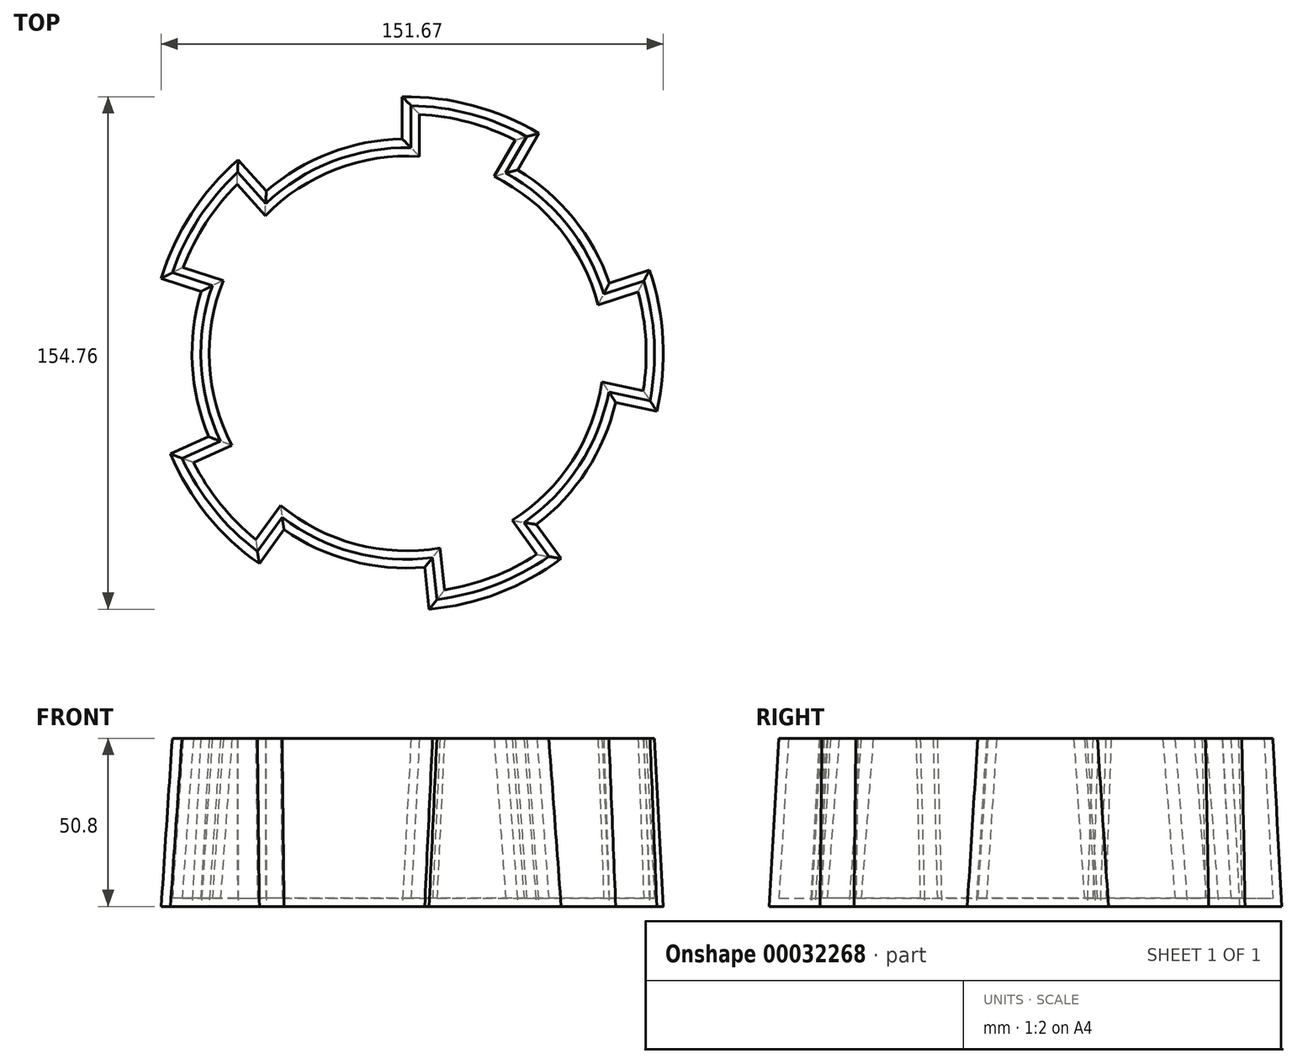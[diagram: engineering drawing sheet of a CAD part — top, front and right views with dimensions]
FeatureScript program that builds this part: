
annotation { "Feature Type Name" : "Feature", "Feature Type Description" : "" }
export const myFeature = defineFeature(function(context is Context, id is Id, definition is map)
    precondition{}
    {
        {
            var Q0;
            Q0=qCreatedBy(makeId("Top.planeOp"),FACE);
            var sketch = newSketch(context, id + "F0", { "sketchPlane" : qUnion([Q0])});
            skArc(sketch, "E0", {"start": v(0, 63.5) * mm, "mid": v(-22.76, 59.28) * mm, "end": v(-42.49, 47.19) * mm});
            skArc(sketch, "E1.0", {"start": v(38.1, 66) * mm, "mid": v(19.72, 73.6) * mm, "end": v(0, 76.2) * mm});
            skLineSegment(sketch, "E2", {"start": v(31.75, 55) * mm, "end": v(38.1, 66) * mm});
            skLineSegment(sketch, "E3", {"start": v(0, 63.5) * mm, "end": v(0, 76.2) * mm});
            skArc(sketch, "E4.1.0", {"start": v(-50.99, 56.63) * mm, "mid": v(-63.9, 41.5) * mm, "end": v(-72.47, 23.55) * mm});
            skLineSegment(sketch, "E4.1.1", {"start": v(-42.49, 47.19) * mm, "end": v(-50.99, 56.63) * mm});
            skLineSegment(sketch, "E4.1.2", {"start": v(-60.4, 19.62) * mm, "end": v(-72.47, 23.55) * mm});
            skArc(sketch, "E4.2.0", {"start": v(-69.61, -31) * mm, "mid": v(-59.22, -47.95) * mm, "end": v(-44.79, -61.65) * mm});
            skLineSegment(sketch, "E4.2.1", {"start": v(-58.01, -25.83) * mm, "end": v(-69.61, -31) * mm});
            skLineSegment(sketch, "E4.2.2", {"start": v(-37.32, -51.37) * mm, "end": v(-44.79, -61.65) * mm});
            skArc(sketch, "E5.1.3.0", {"start": v(7.97, -75.78) * mm, "mid": v(27.3, -71.14) * mm, "end": v(44.79, -61.65) * mm});
            skLineSegment(sketch, "E5.4.3.0", {"start": v(6.64, -63.15) * mm, "end": v(7.97, -75.78) * mm});
            skLineSegment(sketch, "E5.7.3.0", {"start": v(37.32, -51.37) * mm, "end": v(44.79, -61.65) * mm});
            skArc(sketch, "E5.1.4.0", {"start": v(74.53, -15.84) * mm, "mid": v(76.1, 3.99) * mm, "end": v(72.47, 23.55) * mm});
            skLineSegment(sketch, "E5.4.4.0", {"start": v(62.11, -13.2) * mm, "end": v(74.53, -15.84) * mm});
            skLineSegment(sketch, "E5.7.4.0", {"start": v(60.4, 19.62) * mm, "end": v(72.47, 23.55) * mm});
            skArc(sketch, "E6.trimOffspring", {"start": v(-60.4, 19.62) * mm, "mid": v(-63.41, -3.32) * mm, "end": v(-58.01, -25.83) * mm});
            skArc(sketch, "E7.trimOffspring", {"start": v(-37.32, -51.37) * mm, "mid": v(-16.44, -61.34) * mm, "end": v(6.64, -63.15) * mm});
            skArc(sketch, "E8.trimOffspring", {"start": v(37.32, -51.37) * mm, "mid": v(53.26, -34.58) * mm, "end": v(62.11, -13.2) * mm});
            skArc(sketch, "E9.trimOffspring", {"start": v(60.4, 19.62) * mm, "mid": v(49.35, 39.96) * mm, "end": v(31.75, 55) * mm});
            skSolve(sketch);
        }
        {
            var Q0;
            Q0 = qSketchRegion(id + "F0", true);
            extrude(context, id + "F1", {"entities" : qUnion([Q0]), "depth" : 25.4 * mm, "hasDraft" : true, "draftAngle" : 3 * degree, "draftPullDirection" : true, "hasSecondDirection" : true, "secondDirectionOppositeDirection" : true, "secondDirectionDepth" : 25.4 * mm, "hasSecondDirectionDraft" : true, "secondDirectionDraftAngle" : 3 * degree});
        }
        {
            var Q0;
            Q0=makeQuery(id+"F1.opExtrude","CAP_FACE",FACE,{"disambiguationData":[OSD([sQuery(id+"F0.wireOp",EDGE,"E0"),sQuery(id+"F0.wireOp",EDGE,"E1.0"),sQuery(id+"F0.wireOp",EDGE,"E2"),sQuery(id+"F0.wireOp",EDGE,"E3"),sQuery(id+"F0.wireOp",EDGE,"E4.1.0"),sQuery(id+"F0.wireOp",EDGE,"E4.1.1"),sQuery(id+"F0.wireOp",EDGE,"E4.1.2"),sQuery(id+"F0.wireOp",EDGE,"E4.2.0"),sQuery(id+"F0.wireOp",EDGE,"E4.2.1"),sQuery(id+"F0.wireOp",EDGE,"E4.2.2"),sQuery(id+"F0.wireOp",EDGE,"E5.1.3.0"),sQuery(id+"F0.wireOp",EDGE,"E5.4.3.0"),sQuery(id+"F0.wireOp",EDGE,"E5.7.3.0"),sQuery(id+"F0.wireOp",EDGE,"E5.1.4.0"),sQuery(id+"F0.wireOp",EDGE,"E5.4.4.0"),sQuery(id+"F0.wireOp",EDGE,"E5.7.4.0"),sQuery(id+"F0.wireOp",EDGE,"E6.trimOffspring"),sQuery(id+"F0.wireOp",EDGE,"E7.trimOffspring"),sQuery(id+"F0.wireOp",EDGE,"E8.trimOffspring"),sQuery(id+"F0.wireOp",EDGE,"E9.trimOffspring")])],"isStart":false});
            shell(context, id + "F2", {"entities" : qUnion([Q0]), "thickness" : 2.54 * mm});
        }
    });
